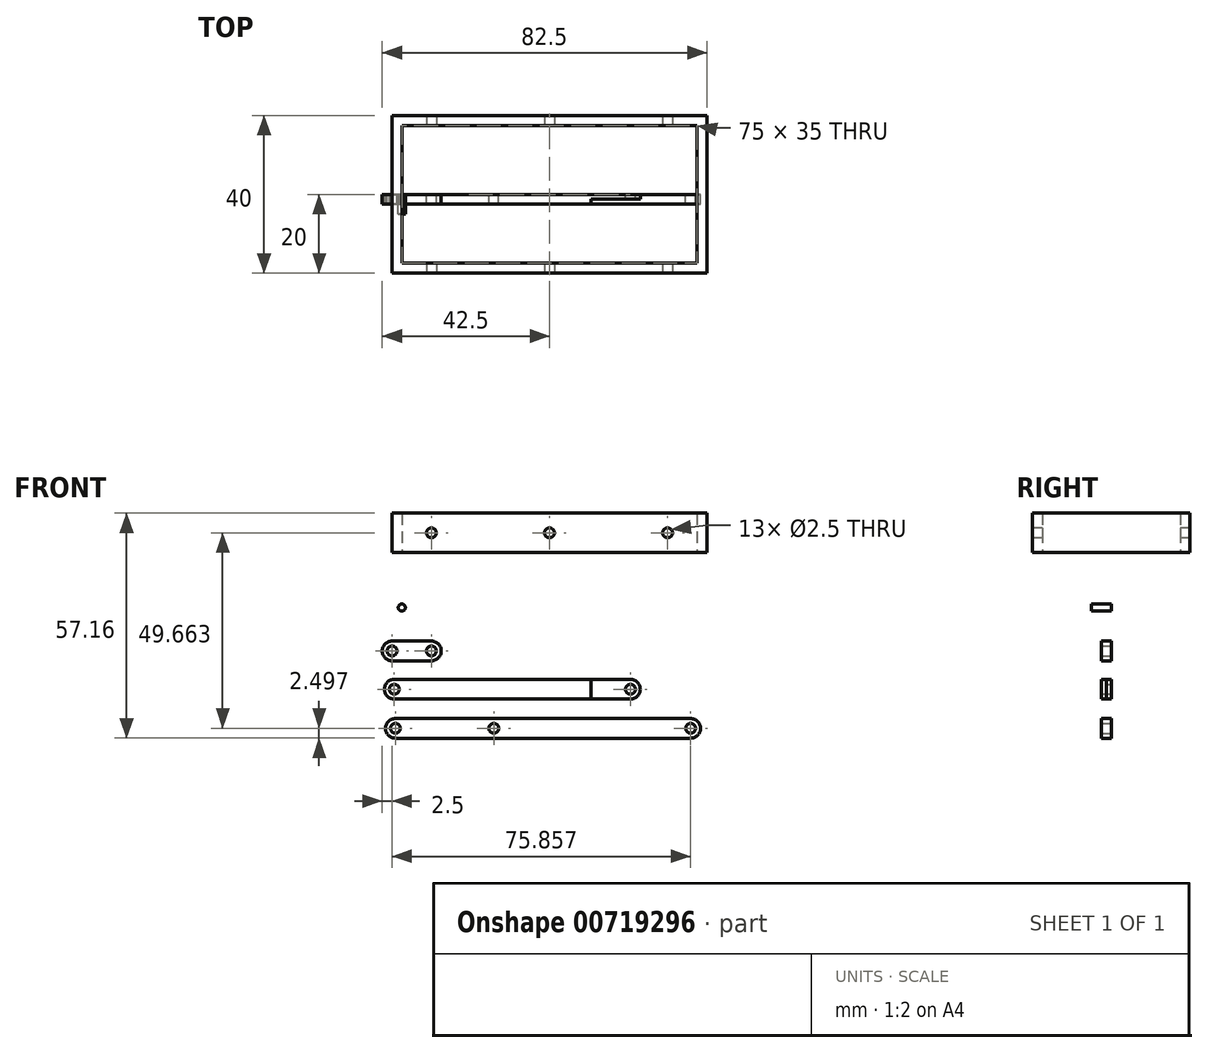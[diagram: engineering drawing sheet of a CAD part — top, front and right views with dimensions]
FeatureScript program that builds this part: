
annotation { "Feature Type Name" : "Feature", "Feature Type Description" : "" }
export const myFeature = defineFeature(function(context is Context, id is Id, definition is map)
    precondition{}
    {
        {
            assignVariable(context, id + "F0", {"name" : "thickness", "anyValue" : 2.5});
        }
        {
            var Q0;
            Q0=qCreatedBy(makeId("Front.planeOp"),FACE);
            var sketch = newSketch(context, id + "F1", { "sketchPlane" : qUnion([Q0])});
            skArc(sketch, "E0", {"start": v(0, 2.5) * mm, "mid": v(-2.5, 0) * mm, "end": v(0, -2.5) * mm});
            skArc(sketch, "E1", {"start": v(10, -2.5) * mm, "mid": v(12.5, 0) * mm, "end": v(10, 2.5) * mm});
            skLineSegment(sketch, "E2", {"start": v(0, 2.5) * mm, "end": v(10, 2.5) * mm});
            skLineSegment(sketch, "E3", {"start": v(0, -2.5) * mm, "end": v(10, -2.5) * mm});
            skCircle(sketch, "E4", {"center": v(0, 0) * mm, "radius": 1.25 * mm});
            skCircle(sketch, "E5", {"center": v(10, 0) * mm, "radius": 1.25 * mm});
            skSolve(sketch);
        }
        {
            var Q0;
            Q0=makeQuery(id+"F1.imprint","IMPRINT",FACE,{"disambiguationData":[TD([[makeQuery(id+"F1.imprint","IMPRINT",EDGE,{"derivedFrom":sQuery(id+"F1.wireOp",EDGE,"E0")}),1.0]])]});
            extrude(context, id + "F2", {"entities" : qUnion([Q0]), "depth" : (getVariable(context, 'thickness')) * mm, "offsetDistance" : 25 * mm});
        }
        {
            var Q0;
            Q0=qCreatedBy(makeId("Front.planeOp"),FACE);
            var sketch = newSketch(context, id + "F3", { "sketchPlane" : qUnion([Q0])});
            skArc(sketch, "E6", {"start": v(0.57, -7.23) * mm, "mid": v(-1.93, -9.73) * mm, "end": v(0.57, -12.23) * mm});
            skArc(sketch, "E7", {"start": v(60.57, -12.23) * mm, "mid": v(63.07, -9.73) * mm, "end": v(60.57, -7.23) * mm});
            skLineSegment(sketch, "E8", {"start": v(0.57, -7.23) * mm, "end": v(60.57, -7.23) * mm});
            skLineSegment(sketch, "E9", {"start": v(0.57, -12.23) * mm, "end": v(60.57, -12.23) * mm});
            skCircle(sketch, "E10", {"center": v(0.57, -9.73) * mm, "radius": 1.25 * mm});
            skCircle(sketch, "E11", {"center": v(60.57, -9.73) * mm, "radius": 1.25 * mm});
            skSolve(sketch);
        }
        {
            var Q0;
            Q0=makeQuery(id+"F3.imprint","IMPRINT",FACE,{"disambiguationData":[TD([[makeQuery(id+"F3.imprint","IMPRINT",EDGE,{"derivedFrom":sQuery(id+"F3.wireOp",EDGE,"E6")}),1.0]])]});
            extrude(context, id + "F4", {"entities" : qUnion([Q0]), "depth" : (getVariable(context, 'thickness')) * mm, "offsetDistance" : 25 * mm});
        }
        {
            var Q0;
            Q0=qCreatedBy(makeId("Front.planeOp"),FACE);
            var sketch = newSketch(context, id + "F5", { "sketchPlane" : qUnion([Q0])});
            skArc(sketch, "E12", {"start": v(0.86, -17.16) * mm, "mid": v(-1.64, -19.66) * mm, "end": v(0.86, -22.16) * mm});
            skArc(sketch, "E13", {"start": v(75.86, -22.16) * mm, "mid": v(78.36, -19.66) * mm, "end": v(75.86, -17.16) * mm});
            skLineSegment(sketch, "E14", {"start": v(0.86, -17.16) * mm, "end": v(75.86, -17.16) * mm});
            skLineSegment(sketch, "E15", {"start": v(0.86, -22.16) * mm, "end": v(75.86, -22.16) * mm});
            skCircle(sketch, "E16", {"center": v(0.86, -19.66) * mm, "radius": 1.25 * mm});
            skCircle(sketch, "E17", {"center": v(75.86, -19.66) * mm, "radius": 1.25 * mm});
            skCircle(sketch, "E18", {"center": v(25.86, -19.66) * mm, "radius": 1.25 * mm});
            skSolve(sketch);
        }
        {
            var Q0;
            Q0=makeQuery(id+"F5.imprint","IMPRINT",FACE,{"disambiguationData":[TD([[makeQuery(id+"F5.imprint","IMPRINT",EDGE,{"derivedFrom":sQuery(id+"F5.wireOp",EDGE,"E12")}),1.0]])]});
            extrude(context, id + "F6", {"entities" : qUnion([Q0]), "depth" : (getVariable(context, 'thickness')) * mm, "offsetDistance" : 25 * mm});
        }
        {
            var Q0;
            Q0=qCreatedBy(makeId("Top.planeOp"),FACE);
            cPlane(context, id + "F7", {"entities" : qUnion([Q0]), "cplaneType" : CPlaneType.OFFSET, "offset" : 25 * mm, "width" : 150 * mm, "height" : 150 * mm});
        }
        {
            var Q0;
            Q0=qCreatedBy(id+"F7.planeOp",FACE);
            var sketch = newSketch(context, id + "F8", { "sketchPlane" : qUnion([Q0])});
            skLineSegment(sketch, "E19.bottom", {"start": v(0, 20) * mm, "end": v(80, 20) * mm});
            skLineSegment(sketch, "E19.top", {"start": v(0, -20) * mm, "end": v(80, -20) * mm});
            skLineSegment(sketch, "E19.left", {"start": v(0, 20) * mm, "end": v(0, -20) * mm});
            skLineSegment(sketch, "E19.right", {"start": v(80, 20) * mm, "end": v(80, -20) * mm});
            skLineSegment(sketch, "E20.0", {"start": v(2.5, 17.5) * mm, "end": v(77.5, 17.5) * mm});
            skLineSegment(sketch, "E20.1", {"start": v(2.5, 17.5) * mm, "end": v(2.5, -17.5) * mm});
            skLineSegment(sketch, "E20.2", {"start": v(2.5, -17.5) * mm, "end": v(77.5, -17.5) * mm});
            skLineSegment(sketch, "E20.3", {"start": v(77.5, 17.5) * mm, "end": v(77.5, -17.5) * mm});
            skSolve(sketch);
        }
        {
            var Q0;
            Q0=makeQuery(id+"F8.imprint","IMPRINT",FACE,{"disambiguationData":[TD([[makeQuery(id+"F8.imprint","IMPRINT",EDGE,{"derivedFrom":sQuery(id+"F8.wireOp",EDGE,"E19.bottom")}),-1.0]])]});
            extrude(context, id + "F9", {"entities" : qUnion([Q0]), "depth" : 10 * mm, "offsetDistance" : 25 * mm});
        }
        {
            var Q0;
            Q0=makeQuery(id+"F9.opExtrude","SWEPT_FACE",FACE,{"disambiguationData":[OSD([sQuery(id+"F8.wireOp",EDGE,"E19.top")])]});
            var sketch = newSketch(context, id + "F10", { "sketchPlane" : qUnion([Q0])});
            skCircle(sketch, "E21", {"center": v(10, 30) * mm, "radius": 1.25 * mm});
            skCircle(sketch, "E22", {"center": v(70, 30) * mm, "radius": 1.25 * mm});
            skCircle(sketch, "E23", {"center": v(40, 30) * mm, "radius": 1.25 * mm});
            skPoint(sketch, "E23.centerSnap0", {"position": v(40, 25) * mm});
            skSolve(sketch);
        }
        {
            var Q0;
            Q0=qSketchRegion(id+"F10",true);
            extrude(context, id + "F11", {"entities" : qUnion([Q0]), "operationType" : NewBodyOperationType.REMOVE, "endBound" : BoundingType.THROUGH_ALL, "oppositeDirection" : true, "depth" : 25 * mm, "offsetDistance" : 25 * mm});
        }
        {
            var Q0;
            Q0=qCreatedBy(makeId("Front.planeOp"),FACE);
            var sketch = newSketch(context, id + "F12", { "sketchPlane" : qUnion([Q0])});
            skCircle(sketch, "E24", {"center": v(2.49, 11.02) * mm, "radius": 0.9 * mm});
            skSolve(sketch);
        }
        {
            var Q0;
            Q0=makeQuery(id+"F12.imprint","IMPRINT",FACE,{"disambiguationData":[TD([[makeQuery(id+"F12.imprint","IMPRINT",EDGE,{"derivedFrom":sQuery(id+"F12.wireOp",EDGE,"E24")}),1.0]])]});
            extrude(context, id + "F13", {"entities" : qUnion([Q0]), "depth" : (getVariable(context, 'thickness') * 2) * mm, "offsetDistance" : 25 * mm});
        }
        {
            var Q0;
            Q0=makeQuery(id+"F4.opExtrude","CAP_FACE",FACE,{"disambiguationData":[OSD([sQuery(id+"F3.wireOp",EDGE,"E6"),sQuery(id+"F3.wireOp",EDGE,"E7"),sQuery(id+"F3.wireOp",EDGE,"E8"),sQuery(id+"F3.wireOp",EDGE,"E9"),sQuery(id+"F3.wireOp",EDGE,"E10"),sQuery(id+"F3.wireOp",EDGE,"E11")])],"isStart":false});
            var sketch = newSketch(context, id + "F14", { "sketchPlane" : qUnion([Q0])});
            skArc(sketch, "E25.0", {"start": v(60.57, -12.23) * mm, "mid": v(63.07, -9.73) * mm, "end": v(60.57, -7.23) * mm});
            skLineSegment(sketch, "E26", {"start": v(60.57, -7.23) * mm, "end": v(50.57, -7.23) * mm});
            skLineSegment(sketch, "E27", {"start": v(50.57, -7.23) * mm, "end": v(50.57, -12.23) * mm});
            skLineSegment(sketch, "E28", {"start": v(50.57, -12.23) * mm, "end": v(60.57, -12.23) * mm});
            skSolve(sketch);
        }
        {
            var Q0;
            Q0 = qSketchRegion(id + "F14", true);
            extrude(context, id + "F15", {"entities" : qUnion([Q0]), "operationType" : NewBodyOperationType.REMOVE, "oppositeDirection" : true, "depth" : 1.25 * mm, "offsetDistance" : 25 * mm});
        }
    });
